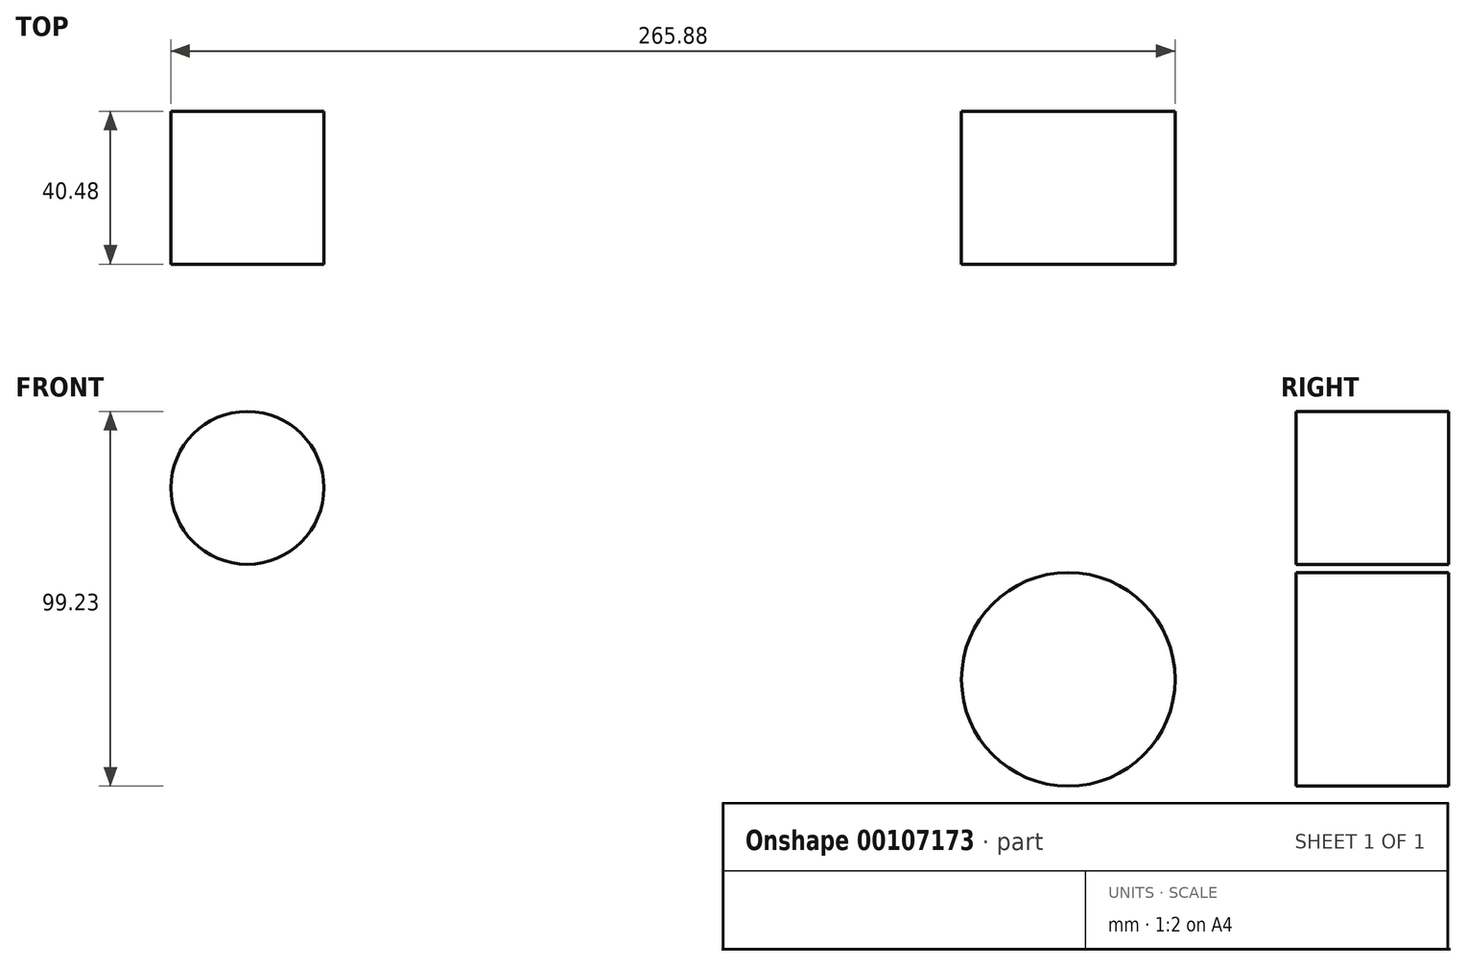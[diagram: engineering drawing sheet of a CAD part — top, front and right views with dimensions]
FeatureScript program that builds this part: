
annotation { "Feature Type Name" : "Feature", "Feature Type Description" : "" }
export const myFeature = defineFeature(function(context is Context, id is Id, definition is map)
    precondition{}
    {
        {
            var Q0;
            Q0=qCreatedBy(makeId("Front.planeOp"),FACE);
            var sketch = newSketch(context, id + "F0", { "sketchPlane" : qUnion([Q0])});
            skCircle(sketch, "E0", {"center": v(90.65, 0) * mm, "radius": 28.27 * mm});
            skCircle(sketch, "E1", {"center": v(-79.1, 2.4) * mm, "radius": 47.6 * mm});
            skCircle(sketch, "E2", {"center": v(-126.72, 50.72) * mm, "radius": 20.24 * mm});
            skSolve(sketch);
        }
        {
            var Q0;
            Q0=makeQuery(id+"F0.imprint","IMPRINT",FACE,{"disambiguationData":[TD([[makeQuery(id+"F0.imprint","IMPRINT",EDGE,{"derivedFrom":sQuery(id+"F0.wireOp",EDGE,"E2")}),1.0]])]});
            var Q1;
            Q1=makeQuery(id+"F0.imprint","IMPRINT",FACE,{"disambiguationData":[TD([[makeQuery(id+"F0.imprint","IMPRINT",EDGE,{"derivedFrom":sQuery(id+"F0.wireOp",EDGE,"E0")}),1.0]])]});
            extrude(context, id + "F1", {"entities" : qUnion([Q0, Q1]), "depth" : 40.48 * mm});
        }
    });
